# Revit family: Electronics_Wireless-Presentation-Systems_Biamp_Modena_Hub-Plus__
name_source: partatom
category: Communication Devices
units: mm (PartAtom-declared; Revit-internal decimal feet)

## family parameters
Cut with Voids When Loaded = No
Host = Face
Maintain Annotation Orientation = No
OmniClass Number = 23.85.10.14
OmniClass Title = Visual Information Systems
Part Type = Normal
Room Calculation Point = No
Round Connector Dimension = Use Diameter
Shared = No

## types (1)
- Hub+
    Altitude = 0-6,600 ft (0-2000m) MSL
    Android = Android 8 or higher
    Apparent Load = 0 VA
    CPU = Intel i5 equivalent or faster
    Connector Description = External power adaptor 12V DC
    Default Elevation = 4' - 0"
    Depth = 0' - 5 3/16"
    Description = Modena™ Hub+ Wireless Presentation Hub
    Height = 0' - 2"
    Housing Material = Biamp - Metal - White
    Humidity = 0-95% relative humidity (non-condensing)
    Mac OSX = Mac OSX 10.11 or higher
    Manufacturer = Biamp
    Max Power Consumption = 0 W
    Media Port = HDMI
    Minimum Bandwidth = 4 Mbps average / 15 Mbps peak per connected client (upstream when presenting; downstream when receiving); Additional 4 Mbps average / 15 Mbps peak for the videoconference host when using the Wireless USB feature
    Model = Modena Hub+
    Network Connection = Ethernet RJ-45 port, 1000 Mbit/s
    Number of Poles = 1
    Power Factor = 1
    Product Documentation Link = https://downloads.biamp.com
    Product Page URL = https://www.biamp.com
    Product data url = https://www.bimobject.com
    Signal Strength = RSSI on connected devices: stable above -65dBm (recommended > - 60dBm); SNR (RSSI - Noise) on connected devices: stable above 25dB (recommended > 35dB)
    Temperature Range = 32 - 104° F (0 – 40° C)
    URL = https://www.biamp.com
    USB Port = USB 2.0/3.0
    Voltage = 12 V
    Web Browser = Chrome, Firefox, Edge
    Weight = 2.40 lbf
    Width = 0' - 6 5/16"
    Windows = Windows 10 .NET; Framework 4.5; Microsoft Direct3D
    Wireless Connection = 2.4Ghz 802.11n compatible Wifi interface; 5Ghz 802.11ac compatible Wifi interface (recommended); Minimum distance between device(s) and access point: ~ 3 feet (~ 1 meter)
    Wireless Presentation Resolution = Up to HD 1080 p at 30 fps
    Wireless USB Feed Resolution = Up to HD 720 p at 30 fps
    iOS = iOS 11 or higher

## geometry (parser evidence)
native form markers: Sweep x1
no freeform markers — native parametric forms only
